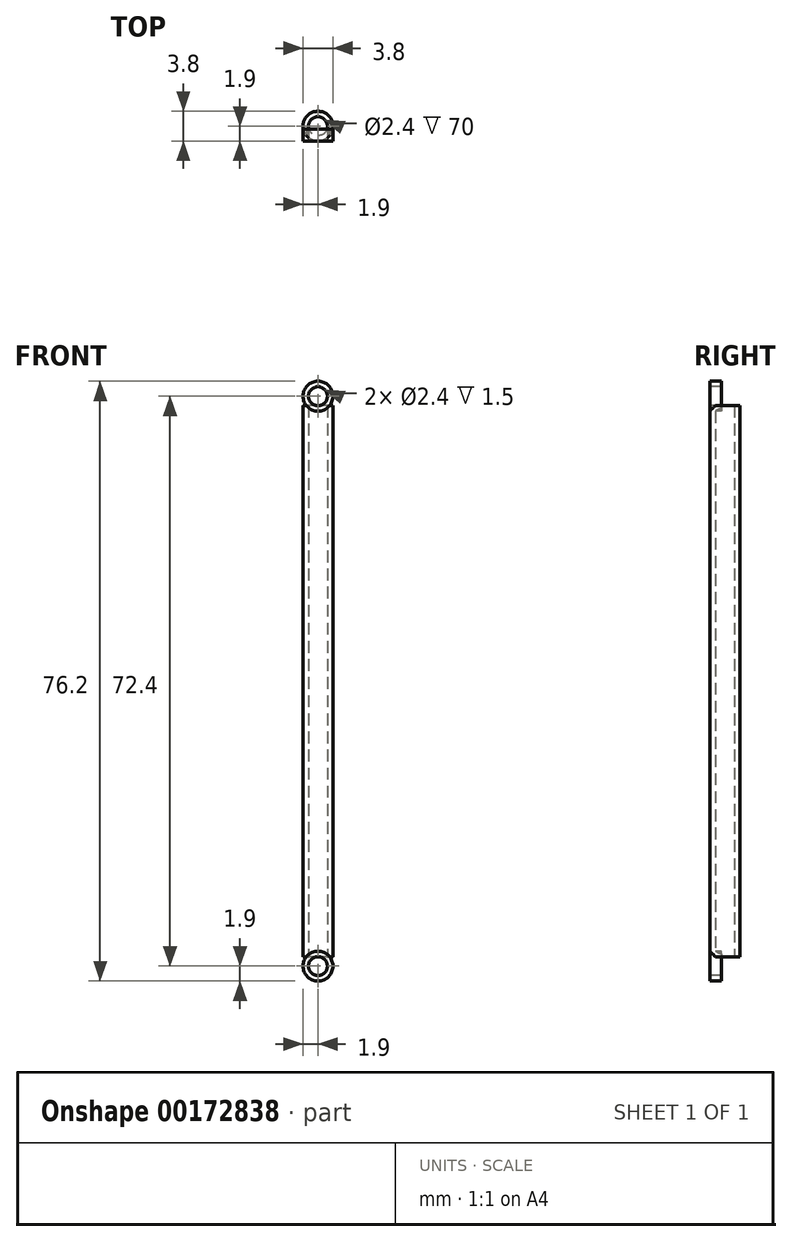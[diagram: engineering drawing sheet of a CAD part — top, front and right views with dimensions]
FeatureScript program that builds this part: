
annotation { "Feature Type Name" : "Feature", "Feature Type Description" : "" }
export const myFeature = defineFeature(function(context is Context, id is Id, definition is map)
    precondition{}
    {
        {
            var Q0;
            Q0=qCreatedBy(makeId("Top.planeOp"),FACE);
            var sketch = newSketch(context, id + "F0", { "sketchPlane" : qUnion([Q0])});
            skCircle(sketch, "E0", {"center": v(0, 1.9) * mm, "radius": 1.9 * mm});
            skCircle(sketch, "E1", {"center": v(0, 1.9) * mm, "radius": 1.2 * mm});
            skSolve(sketch);
        }
        {
            var Q0;
            Q0=makeQuery(id+"F0.imprint","IMPRINT",FACE,{"disambiguationData":[TD([[makeQuery(id+"F0.imprint","IMPRINT",EDGE,{"derivedFrom":sQuery(id+"F0.wireOp",EDGE,"E0")}),1.0]])]});
            extrude(context, id + "F1", {"entities" : qUnion([Q0]), "depth" : 70 * mm});
        }
        {
            var Q0;
            Q0=qCreatedBy(makeId("Front.planeOp"),FACE);
            var sketch = newSketch(context, id + "F2", { "sketchPlane" : qUnion([Q0])});
            skCircle(sketch, "E2", {"center": v(0, -1.2) * mm, "radius": 1.9 * mm});
            skCircle(sketch, "E3", {"center": v(0, -1.2) * mm, "radius": 1.2 * mm});
            skCircle(sketch, "E4", {"center": v(0, 71.2) * mm, "radius": 1.2 * mm});
            skCircle(sketch, "E5", {"center": v(0, 71.2) * mm, "radius": 1.9 * mm});
            skSolve(sketch);
        }
        {
            var Q0;
            Q0=makeQuery(id+"F2.imprint","IMPRINT",FACE,{"disambiguationData":[TD([[makeQuery(id+"F2.imprint","IMPRINT",EDGE,{"derivedFrom":sQuery(id+"F2.wireOp",EDGE,"E4")}),-1.0]])]});
            var Q1;
            Q1=makeQuery(id+"F2.imprint","IMPRINT",FACE,{"disambiguationData":[TD([[makeQuery(id+"F2.imprint","IMPRINT",EDGE,{"derivedFrom":sQuery(id+"F2.wireOp",EDGE,"E2")}),1.0]])]});
            extrude(context, id + "F3", {"entities" : qUnion([Q0, Q1]), "operationType" : NewBodyOperationType.ADD, "oppositeDirection" : true, "depth" : 1.5 * mm});
        }
    });
